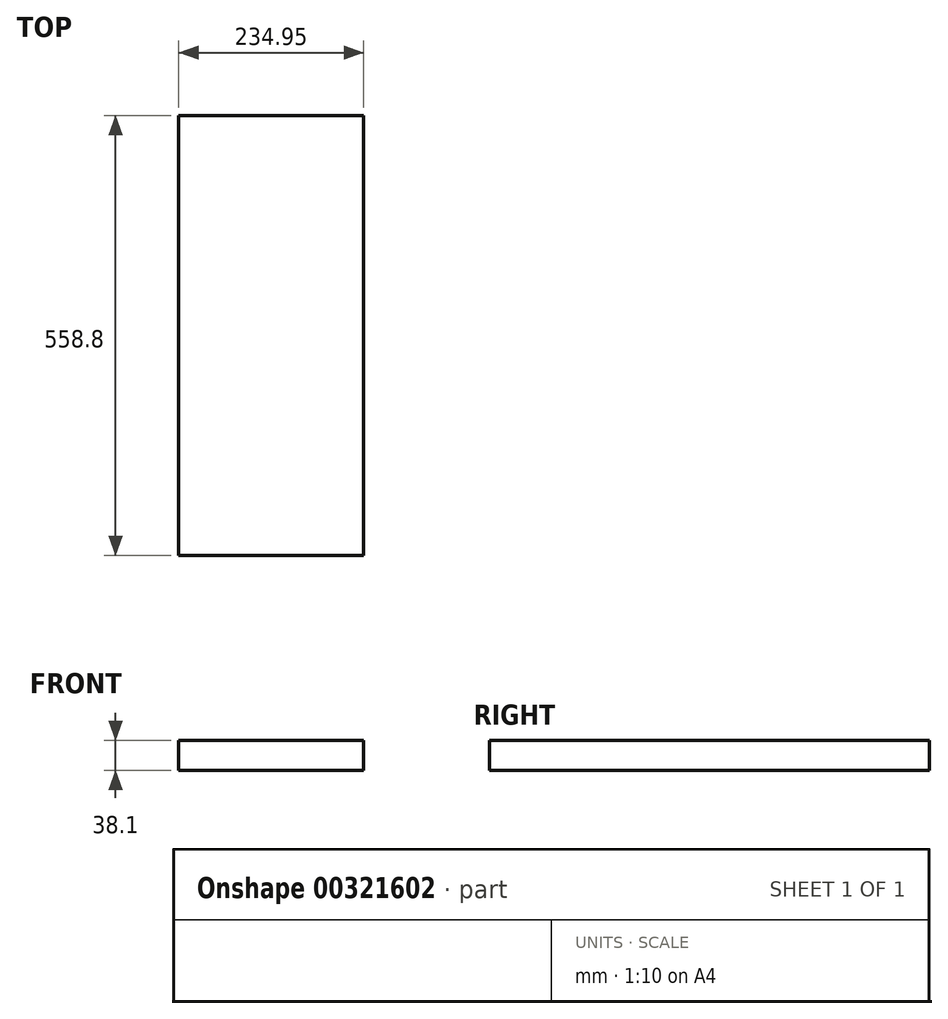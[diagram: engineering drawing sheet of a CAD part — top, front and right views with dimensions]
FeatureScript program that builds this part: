
annotation { "Feature Type Name" : "Feature", "Feature Type Description" : "" }
export const myFeature = defineFeature(function(context is Context, id is Id, definition is map)
    precondition{}
    {
        {
            var Q0;
            Q0=qCreatedBy(makeId("Front.planeOp"),FACE);
            var sketch = newSketch(context, id + "F0", { "sketchPlane" : qUnion([Q0])});
            skLineSegment(sketch, "E0.bottom", {"start": v(-106.89, -13.66) * mm, "end": v(128.06, -13.66) * mm});
            skLineSegment(sketch, "E0.top", {"start": v(-106.89, -51.76) * mm, "end": v(128.06, -51.76) * mm});
            skLineSegment(sketch, "E0.left", {"start": v(-106.89, -13.66) * mm, "end": v(-106.89, -51.76) * mm});
            skLineSegment(sketch, "E0.right", {"start": v(128.06, -13.66) * mm, "end": v(128.06, -51.76) * mm});
            skSolve(sketch);
        }
        {
            var Q0;
            Q0=makeQuery(id+"F0.imprint","IMPRINT",FACE,{"disambiguationData":[TD([[makeQuery(id+"F0.imprint","IMPRINT",EDGE,{"derivedFrom":sQuery(id+"F0.wireOp",EDGE,"E0.bottom")}),-1.0]])]});
            extrude(context, id + "F1", {"entities" : qUnion([Q0]), "depth" : 558.8 * mm});
        }
    });
